# Revit family: Building-IEC309Connections-GEWISS-IEC309HP-10°_FLUSH-MOUNT_SOCKET_63A_IP66-67
name_source: partatom
category: Apparecchi elettrici
units: mm (PartAtom-declared; Revit-internal decimal feet)

## family parameters
Condiviso = No
Host = Superficie
Mantenere orientamento annotazione = Sì
Punto di calcolo locali = Sì
Quota connettore circolare = Usa diametro
Taglio con vuoti quando caricato = No
Tipo di parte = Normale

## types (27) — shared parameters
BLOCCO = B=C
Breaking capacity at 1.1 Un = 79A
Catalogue = BUILDING
Corpo centrale = Default(2)
Electrocod = 2211
FORMULA = 1000 mm  [stored 3.28084 ft]
Flange dimensions (mm) = 110x100
Glow wire test: = 850 °C (active parts) - 650 °C (passive parts)
IDF = 10867db1-7908-4c65-8bee-f1d746e17607
IDT = f31e6adf160a4e7098cc0e80221f4c29
IP degree = IP66/IP67
Immagine tipo = <Nessuno>
Insulation resistance = - 10 M?
L = 155 mm
N.poli = 1
Operating temperature: = -25 +55 °C
Piastra = Default(2)
Produttore = GEWISS S.p.A.
Prospetto di default = 500 mm
Rated current (A) = 63
SEO = Socket outlet
SPinotto = Default(2)
Shock resistance = IK09
Sportello_visibile = Sì
Spostamento_S = 950 mm
Technical sheet = https://www.gewiss.com
Terminal tightening capacity = 6-16mm² flexible cables - 6-25mm² rigid cables
Thermo-pressure with ball = 125 °C (active parts) - 80 °C (passive parts)
Total number of operations = -2000
Type of material = Halogen-free in compliance with EN 60754-2
Type of wiring = Mantle terminal
Typology = 10° angled flush-mounting socket-outlet
URL = https://www.gewiss.com
Version file RFA = 21.11
Voltaggio = 0 V
W = 115 mm

## per-type parameters (varying)
| type | Characteristics | Colour: | Descrizione | Frequency | Modello | No. of poles | Rated voltage: | Reference h |
| GW63253H - 10°FLUSH.S.O.HP IP67 3P+E 63A 400V 6H |  | Red | 10°FLUSH.S.O.HP IP67 3P+E 63A 400V 6H | 50/60 Hz | GW63253H | 3P+E | 380 - 415 V | 6 |
| GW63246H - 10°FLUSH.S.O.HP IP67 2P+E 63A 110V 4H |  | Yellow | 10°FLUSH.S.O.HP IP67 2P+E 63A 110V 4H | 50/60 Hz | GW63246H | 2P+E | 100 - 130 V | 4 |
| GW63258H - 10°FLUSH.S.O.HP IP67 3P+E 63A 690V 5H |  | Black | 10°FLUSH.S.O.HP IP67 3P+E 63A 690V 5H | 50/60 Hz | GW63258H | 3P+E | 600 - 690 V | 5 |
| GW63269H - 10°FLUSH.S.O.HP IP67 2P+E 63A-250Vcc 8H |  | Grey | 10°FLUSH.S.O.HP IP67 2P+E 63A >250Vcc 8H | d.c. | GW63269H | 2P+E | -250 V | 8 |
| GW63259H - 10°FLUSH.S.O.HP IP67 3P+N+E 63A 690V 5H |  | Black | 10°FLUSH.S.O.HP IP67 3P+N+E 63A 690V 5H | 50/60 Hz | GW63259H | 3P+N+E | 600 - 690 V | 5 |
| GW63253PH - 10°FLUSH.S.O.HP IP67 3P+E 63A 400V 6H PC | Pilot contact | Red | 10°FLUSH.S.O.HP IP67 3P+E 63A 400V 6H PC | 50/60 Hz | GW63253PH | 3P+E | 380 - 415 V | 6 |
| GW63264H - 10°FLUSH.S.O.HP IP67 3P+E 63A-50V 2H |  | Green | 10°FLUSH.S.O.HP IP67 3P+E 63A >50V 2H | -300 - 500 Hz | GW63264H | 3P+E | -50 V | 2 |
| GW63266H - 10°FL.S.O.HP IP67 3P+E 63A 440÷460V 11H |  | Red | 10°FL.S.O.HP IP67 3P+E 63A 440÷460V 11H | 60 Hz | GW63266H | 3P+E | 440 - 460 V | 11 |
| GW63248H - 10°FLUSH.S.O.HP IP67 3P+N+E 63A 110V 4H |  | Yellow | 10°FLUSH.S.O.HP IP67 3P+N+E 63A 110V 4H | 50/60 Hz | GW63248H | 3P+N+E | 100 - 130 V | 4 |
| GW63247H - 10°FLUSH.S.O.HP IP67 3P+E 63A 110V 4H |  | Yellow | 10°FLUSH.S.O.HP IP67 3P+E 63A 110V 4H | 50/60 Hz | GW63247H | 3P+E | 100 - 130 V | 4 |
| GW63254H - 10°FLUSH.S.O.HP IP67 3P+N+E 63A 400V 6H |  | Red | 10°FLUSH.S.O.HP IP67 3P+N+E 63A 400V 6H | 50/60 Hz | GW63254H | 3P+N+E | 346 - 415 V | 6 |
| GW63256H - 10°FLUSH.S.O.HP IP67 3P+N+E 63A 500V 7H |  | Black | 10°FLUSH.S.O.HP IP67 3P+N+E 63A 500V 7H | 50/60 Hz | GW63256H | 3P+N+E | 480 - 500 V | 7 |
| GW63265H - 10°FLUSH.S.O.HP IP67 3P+N+E 63A-50V 2H |  | Green | 10°FLUSH.S.O.HP IP67 3P+N+E 63A >50V 2H | -300 - 500 Hz | GW63265H | 3P+N+E | -50 V | 2 |
| GW63267H - 10°FL.S.O.HP IP67 3P+N+E 63A440÷460V11H |  | Red | 10°FL.S.O.HP IP67 3P+N+E 63A440÷460V11H | 60 Hz | GW63267H | 3P+N+E | 440 - 460 V | 11 |
| GW63261H - 10°FLUSH.S.O.HP IP67 3P+E 63A-50V 10H |  | Green | 10°FLUSH.S.O.HP IP67 3P+E 63A >50V 10H | 100 - 300 Hz | GW63261H | 3P+E | -50 V | 10 |
| GW63268H - 10°FL.S.O.HP IP67 2P+E 63A-50÷250Vcc3H |  | Grey | 10°FL.S.O.HP IP67 2P+E 63A >50÷250Vcc3H | d.c. | GW63268H | 2P+E | -50 - 250 V | 3 |
| GW63250H - 10°FLUSH.S.O.HP IP67 3P+E 63A 230V 9H |  | Blue | 10°FLUSH.S.O.HP IP67 3P+E 63A 230V 9H | 50/60 Hz | GW63250H | 3P+E | 200 - 250 V | 9 |
| GW63251H - 10°FLUSH.S.O.HP IP67 3P+N+E 63A 230V 9H |  | Blue | 10°FLUSH.S.O.HP IP67 3P+N+E 63A 230V 9H | 50/60 Hz | GW63251H | 3P+N+E | 200 - 250 V | 9 |
| GW63262H - 10°FLUSH.S.O.HP IP67 3P+N+E 63A-50V 10H |  | Green | 10°FLUSH.S.O.HP IP67 3P+N+E 63A >50V 10H | 100 - 300 Hz | GW63262H | 3P+N+E | -50 V | 10 |
| GW63254PH - 10°FL.S.O.HP IP67 3P+N+E 63A 400V 6H PC | Pilot contact | Red | 10°FL.S.O.HP IP67 3P+N+E 63A 400V 6H PC | 50/60 Hz | GW63254PH | 3P+N+E | 346 - 415 V | 6 |
| GW63249H - 10°FLUSH.S.O.HP IP67 2P+E 63A 230V 6H |  | Blue | 10°FLUSH.S.O.HP IP67 2P+E 63A 230V 6H | 50/60 Hz | GW63249H | 2P+E | 200 - 250 V | 6 |
| GW63252H - 10°FLUSH.S.O.HP IP67 2P+E 63A 400V 9H |  | Red | 10°FLUSH.S.O.HP IP67 2P+E 63A 400V 9H | 50/60 Hz | GW63252H | 2P+E | 380 - 415 V | 9 |
| GW63257H - 10°FLUSH.S.O.HP IP67 2P+E 63A 500V 7H |  | Black | 10°FLUSH.S.O.HP IP67 2P+E 63A 500V 7H | 50/60 Hz | GW63257H | 2P+E | 480 - 500 V | 7 |
| GW63263H - 10°FLUSH.S.O.HP IP67 2P+E 63A-50V 2H |  | Green | 10°FLUSH.S.O.HP IP67 2P+E 63A >50V 2H | -300 - 500 Hz | GW63263H | 2P+E | -50 V | 2 |
| GW63255H - 10°FLUSH.S.O.HP IP67 3P+E 63A 500V 7H |  | Black | 10°FLUSH.S.O.HP IP67 3P+E 63A 500V 7H | 50/60 Hz | GW63255H | 3P+E | 480 - 500 V | 7 |
| GW63260H - 10°FLUSH.S.O.HP IP67 2P+E 63A-50V 10H |  | Green | 10°FLUSH.S.O.HP IP67 2P+E 63A >50V 10H | 100 - 300 Hz | GW63260H | 2P+E | -50 V | 10 |
| GW63249PH - 10°FLUSH.S.O.HP IP67 2P+E 63A 230V 6H PC | Pilot contact | Blue | 10°FLUSH.S.O.HP IP67 2P+E 63A 230V 6H PC | 50/60 Hz | GW63249PH | 2P+E | 200 - 250 V | 6 |

note: [stored X ft] marks values corroborated as IEEE doubles in the binary element streams (Revit-internal decimal feet)

## geometry (parser evidence)
native form markers: Sweep x2
no freeform markers — native parametric forms only
